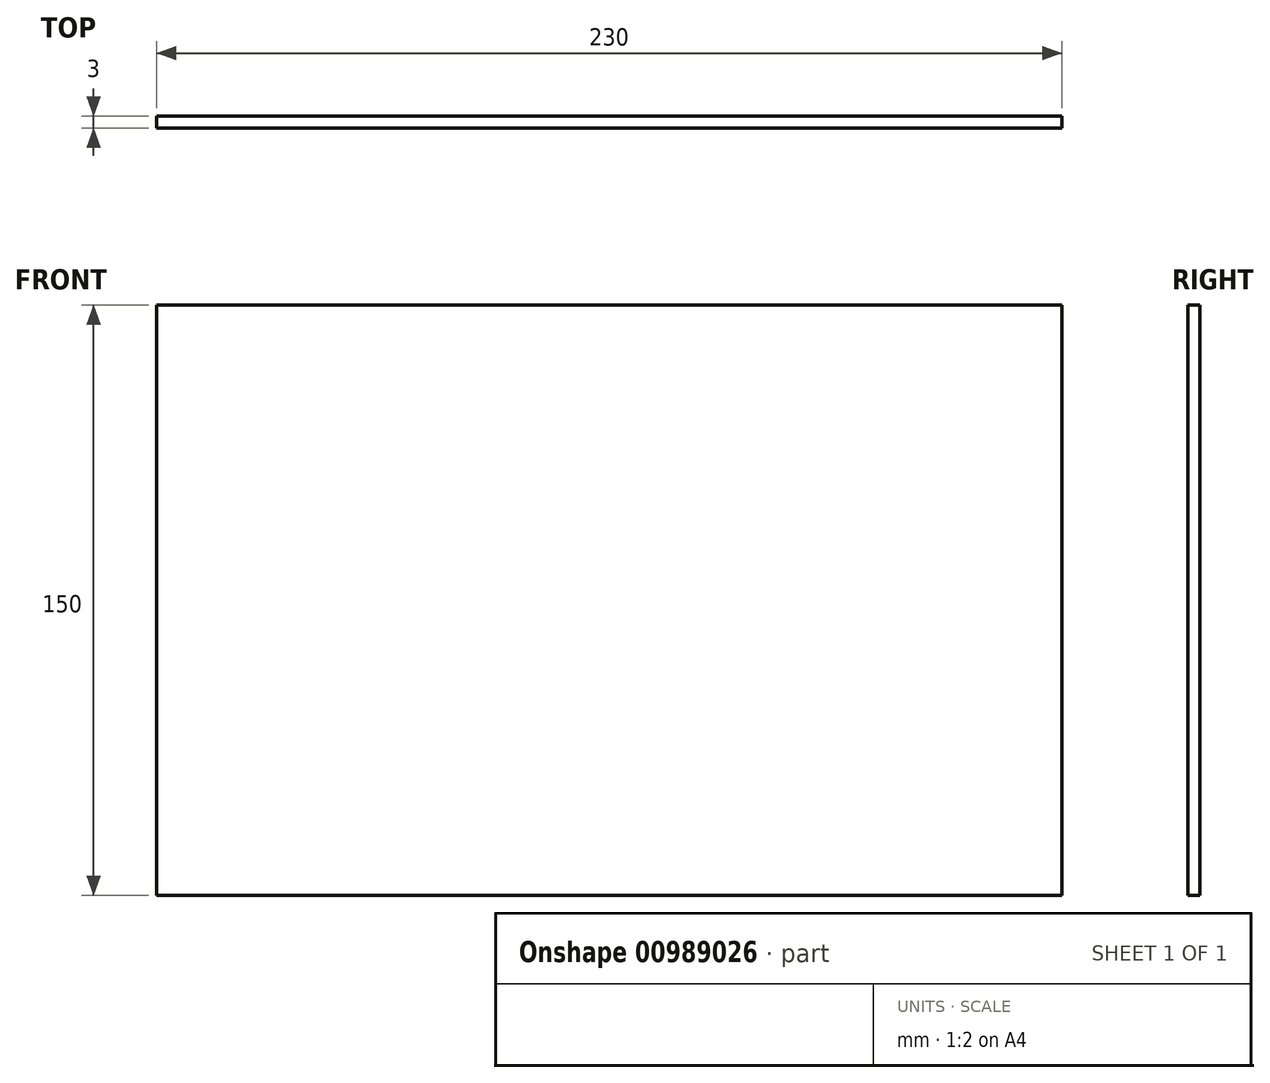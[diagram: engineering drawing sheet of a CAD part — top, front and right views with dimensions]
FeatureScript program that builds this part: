
annotation { "Feature Type Name" : "Feature", "Feature Type Description" : "" }
export const myFeature = defineFeature(function(context is Context, id is Id, definition is map)
    precondition{}
    {
        {
            var Q0;
            Q0=qCreatedBy(makeId("Front.planeOp"),FACE);
            var sketch = newSketch(context, id + "F0", { "sketchPlane" : qUnion([Q0])});
            skLineSegment(sketch, "E0.bottom", {"start": v(-115, 75) * mm, "end": v(115, 75) * mm});
            skLineSegment(sketch, "E0.top", {"start": v(-115, -75) * mm, "end": v(115, -75) * mm});
            skLineSegment(sketch, "E0.left", {"start": v(-115, 75) * mm, "end": v(-115, -75) * mm});
            skLineSegment(sketch, "E0.right", {"start": v(115, 75) * mm, "end": v(115, -75) * mm});
            skLineSegment(sketch, "E1", {"start": v(-115, 75) * mm, "end": v(115, -75) * mm, "construction": true});
            skSolve(sketch);
        }
        {
            var Q0;
            Q0 = qSketchRegion(id + "F0", true);
            extrude(context, id + "F1", {"entities" : qUnion([Q0]), "depth" : 3 * mm, "offsetDistance" : 25 * mm});
        }
    });
